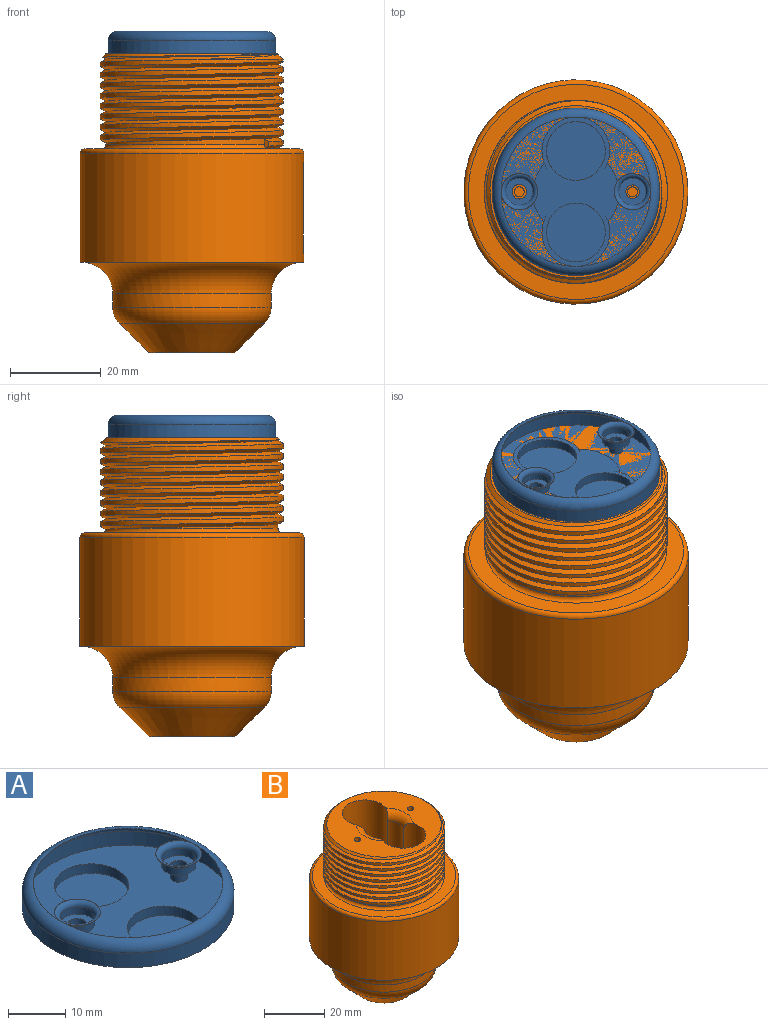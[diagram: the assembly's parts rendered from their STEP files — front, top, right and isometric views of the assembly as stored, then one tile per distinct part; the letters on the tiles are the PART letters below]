
ASSEMBLY  parts=2 mates=1
PART A: 16 faces, bbox 40x40x7 mm
  f0: cylinder r=1.5mm len=3mm, axis (0,0,1), area 23.6mm2, adj f4,f8
  f1: cylinder r=1.61mm len=3.22mm, axis (0,0,1), area 25.3mm2, adj f4,f6
  f2: cylinder r=18.5mm len=37mm, axis (0,0,-1), area 348.7mm2, adj f4,f9
  f3: plane 33x33mm, normal (0,0,1), area 754.8mm2, adj f9,f10,f11
  f4: plane 37x37mm, normal (0,0,-1), area 794.5mm2, adj f0,f1,f2,f12,f14
  f5: cylinder r=3mm len=6mm, axis (0,0,1), area 28.3mm2, adj f6,f11
  f6: plane 6x6mm, normal (0,0,1), area 20.1mm2, adj f1,f5
  f7: cylinder r=3mm len=6mm, axis (0,0,1), area 28.3mm2, adj f8,f10
  f8: plane 6x6mm, normal (0,0,1), area 21.2mm2, adj f0,f7
  f9: torus R=16.5mm, axis (0,0,1), area 350.8mm2, adj f2,f3
  f10: torus R=4mm, axis (0,0,1), area 33.2mm2, adj f3,f7
  f11: torus R=4mm, axis (0,0,1), area 33.2mm2, adj f3,f5
  f12: cylinder r=6.5mm len=13mm, axis (0,0,1), area 81.7mm2, adj f4,f13
  f13: plane 13x13mm, normal (0,0,-1), area 132.7mm2, adj f12
  f14: cylinder r=6.5mm len=13mm, axis (0,0,1), area 81.7mm2, adj f4,f15
  f15: plane 13x13mm, normal (0,0,-1), area 132.7mm2, adj f14
PART B: 51 faces, bbox 53.7x53.7x67.3 mm
  f0: cylinder r=6.5mm len=7.44mm, axis (0,0,1), area 4mm2, adj f17,f19,f28,f43
  f1: cylinder r=6.5mm len=20.5mm, axis (0,0,1), area 162.5mm2, adj f17,f19,f42,f45
  f2: plane 6x4.5mm, normal (1,0,0), area 24.2mm2, adj f29,f30,f32,f34,f38
  f3: cylinder r=3.15mm len=19mm, axis (0,0,1), area 261mm2, adj f17,f18,f19,f20,f21,f27,f28
  f4: bspline ~48.73x42.2mm, area 1479.4mm2, adj f6,f8,f9,f13,f46
  f5: bspline ~48.73x42.2mm, area 1370.6mm2, adj f6,f8,f9,f46
  f6: cylinder r=19mm len=38mm, axis (0,0,-1), area -22.9mm2, adj f4,f5,f7,f8,f13
  f7: plane 38x38mm, normal (0,0,1), area 650.1mm2, adj f6,f9,f17,f19,f44,f45,f47,f49
  f8: plane 2.09x1.03mm, normal (-0.54,-0.84,0), area 1.9mm2, adj f4,f5,f6,f13,f46
  f9: cone r=19mm half-angle=45deg, axis (0,0,-1), area 149.9mm2, adj f4,f5,f7,f46
  f10: cylinder r=24.76mm len=49.52mm, axis (0,0,1), area 3613.4mm2, adj f11,f14,f29,f30,f31,f32
  f11: plane 49.52x49.52mm, normal (0,0,-1), area 40.2mm2, adj f10,f24
  f12: plane 47.52x47.52mm, normal (0,0,1), area 516.9mm2, adj f13,f14
  f13: torus R=20mm, axis (0,0,1), area 167.5mm2, adj f4,f6,f8,f12
  f14: torus R=23.76mm, axis (0,0,1), area 240.8mm2, adj f10,f12
  f15: plane 19x19mm, normal (0,0,-1), area 267.6mm2, adj f22,f23
  f16: cylinder r=17.5mm len=35mm, axis (0,0,1), area 322.1mm2, adj f24,f25
  f17: cylinder r=7.5mm len=55mm, axis (0,0,1), area 1985.4mm2, adj f0,f1,f3,f7,f18,f26,f27,f28
  f18: plane 15x14.57mm, normal (0,0,1), area 171mm2, adj f3,f17
  f19: cylinder r=7.5mm len=55mm, axis (0,0,1), area 2014.8mm2, adj f0,f1,f3,f7,f20,f26,f27,f28
  f20: plane 15x14.57mm, normal (0,0,1), area 171mm2, adj f3,f19
  f21: plane 6.3x6.3mm, normal (0,0,1), area 15.3mm2, adj f3,f22
  f22: cylinder r=2.25mm len=4.5mm, axis (0,0,-1), area 28.3mm2, adj f15,f21
  f23: cone r=17.5mm half-angle=45deg, axis (0,0,1), area 741.5mm2, adj f15,f25
  f24: torus R=24.5mm, axis (0,0,1), area 1384.8mm2, adj f11,f16
  f25: torus R=12.5mm, axis (0,0,-1), area 419.5mm2, adj f16,f23
  f26: cylinder r=6.5mm len=42mm, axis (0,0,1), area 333mm2, adj f17,f19,f27,f44
  f27: plane 7.44x4.01mm, normal (0,0,1), area 19.3mm2, adj f3,f17,f19,f26
  f28: plane 7.44x4.01mm, normal (0,0,1), area 19.3mm2, adj f0,f3,f17,f19
  f29: plane 6x3.76mm, normal (0,0,-1), area 22.2mm2, adj f2,f10,f30,f32
  f30: plane 20.07x16.12mm, normal (0,1,0), area 210mm2, adj f2,f10,f29,f31,f33,f34,f35,f40
  f31: plane 6x3.76mm, normal (0,0,1), area 22.2mm2, adj f10,f30,f32,f33
  f32: plane 20.11x16.7mm, normal (0,-1,0), area 216.6mm2, adj f2,f10,f29,f31,f33,f34,f35,f41
  f33: plane 6x4.5mm, normal (1,0,0), area 24.2mm2, adj f30,f31,f32,f35,f36
  f34: plane 9.98x6mm, normal (0,0,-1), area 57.8mm2, adj f2,f30,f32,f42
  f35: plane 9.98x6mm, normal (0,0,1), area 57.8mm2, adj f30,f32,f33,f43
  f36: cylinder r=0.95mm len=8mm, axis (1,0,0), area 47.8mm2, adj f33,f37
  f37: plane 1.9x1.9mm, normal (1,0,0), area 2.8mm2, adj f36
  f38: cylinder r=0.95mm len=8mm, axis (1,0,0), area 47.8mm2, adj f2,f39
  f39: plane 1.9x1.9mm, normal (1,0,0), area 2.8mm2, adj f38
  f40: cylinder r=5mm len=18.37mm, axis (0,0,1), area 48.8mm2, adj f17,f30,f42,f43
  f41: cylinder r=5mm len=18.21mm, axis (0,0,1), area 42.9mm2, adj f19,f32,f42,f43
  f42: torus R=11.5mm, axis (0,0,-1), area 54.7mm2, adj f1,f17,f19,f30,f32,f34,f40,f41
  f43: torus R=11.5mm, axis (0,0,-1), area 54.7mm2, adj f0,f17,f19,f30,f32,f35,f40,f41
  f44: torus R=9.5mm, axis (0,0,1), area 48.5mm2, adj f7,f17,f19,f26
  f45: torus R=9.5mm, axis (0,0,1), area 48.5mm2, adj f1,f7,f17,f19
  f46: bspline ~40.56x40.56mm, area 984.3mm2, adj f4,f5,f8,f9
  f47: cylinder r=1.1mm len=20mm, axis (0,0,1), area 138.2mm2, adj f7,f48
  f48: plane 2.2x2.2mm, normal (0,0,1), area 3.8mm2, adj f47
  f49: cylinder r=1.1mm len=20mm, axis (0,0,1), area 138.2mm2, adj f7,f50
  f50: plane 2.2x2.2mm, normal (0,0,1), area 3.8mm2, adj f49
PLACE A t=(-7.41,-12.1,20.68)mm
PLACE B t=(-7.41,-12.1,-0.32)mm
MATE fastened A.f1 <-> B.f47  axis (0,0,-1) through (-19.91,-12.1,20.68)mm
